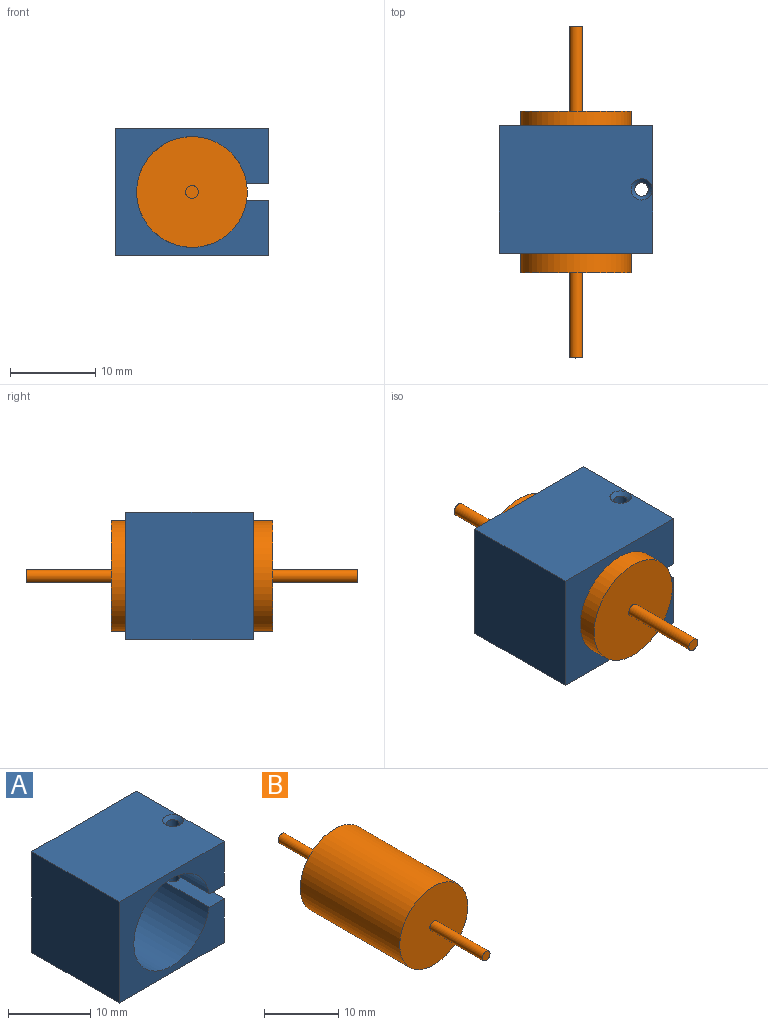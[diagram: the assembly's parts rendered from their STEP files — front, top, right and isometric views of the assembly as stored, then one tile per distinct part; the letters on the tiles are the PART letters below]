
ASSEMBLY  parts=2 mates=1
PART A: 13 faces, bbox 18x15x15 mm
  f0: plane 15x6.5mm, normal (1,0,0), area 97.5mm2, adj f1,f3,f5,f9
  f1: plane 18x15mm, normal (0,-1,0), area 132.2mm2, adj f0,f2,f4,f5,f6,f7,f8,f9
  f2: plane 15x6.5mm, normal (1,0,0), area 97.5mm2, adj f1,f3,f6,f8
  f3: plane 18x15mm, normal (0,1,0), area 132.2mm2, adj f0,f2,f4,f5,f6,f7,f8,f9
  f4: plane 15x15mm, normal (-1,0,0), area 225mm2, adj f1,f3,f5,f6
  f5: plane 18x15mm, normal (0,0,1), area 265.1mm2, adj f0,f1,f3,f4,f11
  f6: plane 18x15mm, normal (0,0,-1), area 268mm2, adj f1,f2,f3,f4,f12
  f7: cylinder r=6.5mm len=15mm, axis (0,-1,0), area 582.5mm2, adj f1,f3,f8,f9
  f8: plane 15x2.58mm, normal (0,0,1), area 36.7mm2, adj f1,f2,f3,f7,f12
  f9: plane 15x2.58mm, normal (0,0,-1), area 36.7mm2, adj f0,f1,f3,f7,f10
  f10: cylinder r=0.8mm len=6.05mm, axis (0,0,1), area 30.4mm2, adj f9,f11
  f11: cone r=0.8mm half-angle=45deg, axis (0,0,1), area 4.1mm2, adj f5,f10
  f12: cylinder r=0.8mm len=6.5mm, axis (0,0,1), area 32.7mm2, adj f6,f8
PART B: 7 faces, bbox 13x39x13 mm
  f0: cylinder r=6.5mm len=19mm, axis (0,1,0), area 776mm2, adj f1,f2
  f1: plane 13x13mm, normal (0,-1,0), area 131mm2, adj f0,f5
  f2: plane 13x13mm, normal (0,1,0), area 131mm2, adj f0,f4
  f3: plane 1.5x1.5mm, normal (0,1,0), area 1.8mm2, adj f4
  f4: cylinder r=0.75mm len=10mm, axis (0,1,0), area 47.1mm2, adj f2,f3
  f5: cylinder r=0.75mm len=10mm, axis (0,1,0), area 47.1mm2, adj f1,f6
  f6: plane 1.5x1.5mm, normal (0,-1,0), area 1.8mm2, adj f5
PLACE A t=(-12.28,-9.02,3.22)mm fixed
PLACE B rot(axis=(0,-1,0),6.1deg) t=(-12.28,0.19,10.72)mm
MATE cylindrical A.f7 <-> B.f0  axis (0,-1,0) through (-12.28,-16.52,10.72)mm
